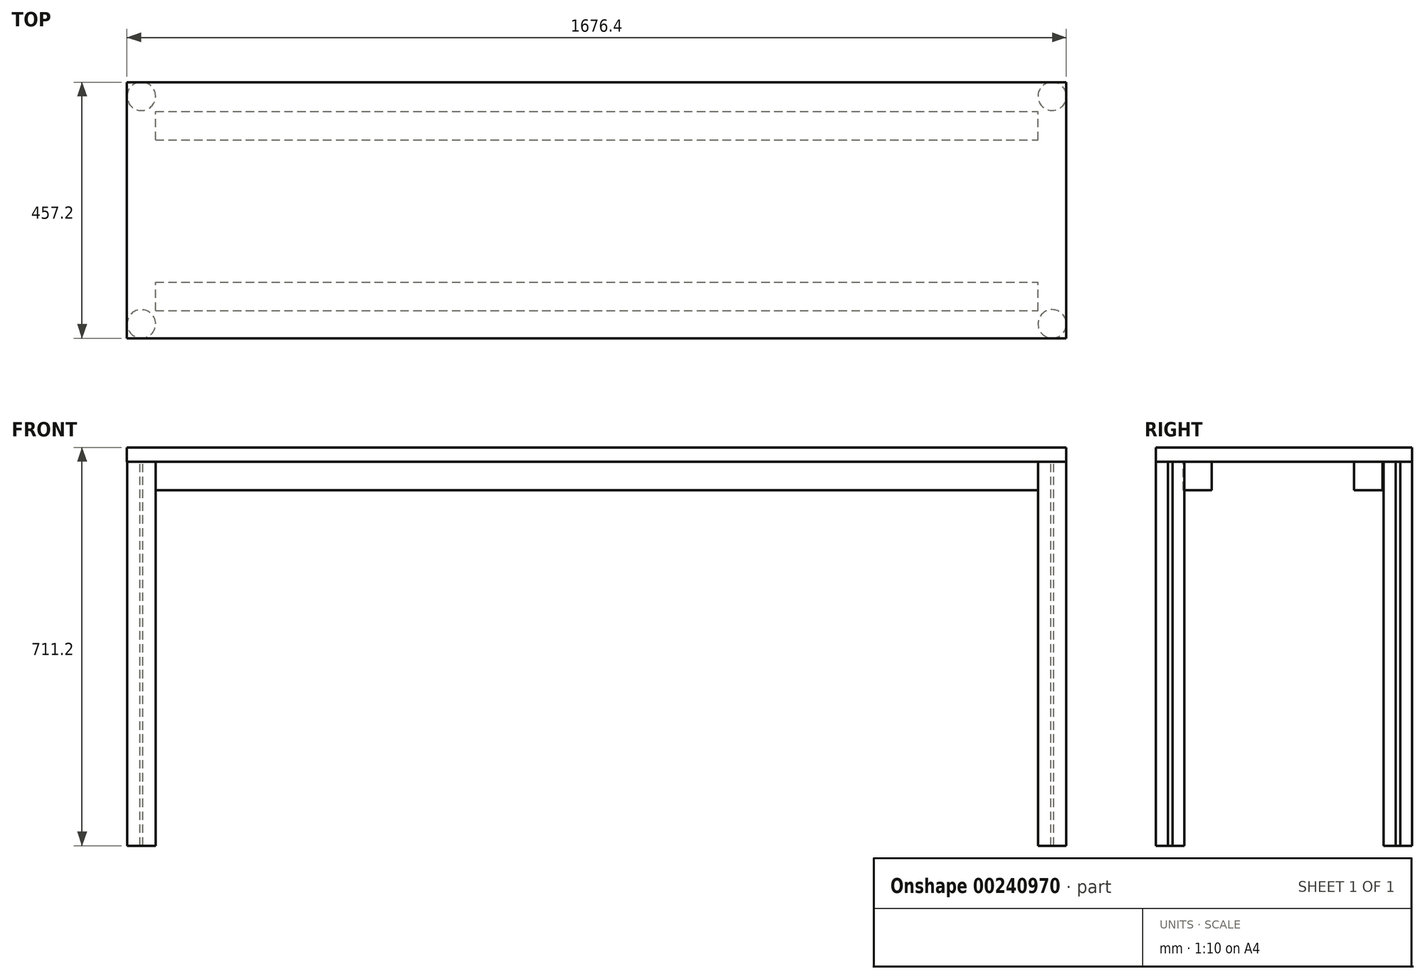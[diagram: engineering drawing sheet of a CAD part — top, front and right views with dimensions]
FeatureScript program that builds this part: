
annotation { "Feature Type Name" : "Feature", "Feature Type Description" : "" }
export const myFeature = defineFeature(function(context is Context, id is Id, definition is map)
    precondition{}
    {
        {
            var Q0;
            Q0=qCreatedBy(makeId("Top.planeOp"),FACE);
            var sketch = newSketch(context, id + "F0", { "sketchPlane" : qUnion([Q0])});
            skLineSegment(sketch, "E0.bottom", {"start": v(-1681, -104.49) * mm, "end": v(-4.6, -104.49) * mm});
            skLineSegment(sketch, "E0.top", {"start": v(-1681, -561.69) * mm, "end": v(-4.6, -561.69) * mm});
            skLineSegment(sketch, "E0.left", {"start": v(-1681, -104.49) * mm, "end": v(-1681, -561.69) * mm});
            skLineSegment(sketch, "E0.right", {"start": v(-4.6, -104.49) * mm, "end": v(-4.6, -561.69) * mm});
            skSolve(sketch);
        }
        {
            var Q0;
            Q0=makeQuery(id+"F0.imprint","IMPRINT",FACE,{"disambiguationData":[TD([[makeQuery(id+"F0.imprint","IMPRINT",EDGE,{"derivedFrom":sQuery(id+"F0.wireOp",EDGE,"E0.bottom")}),-1.0]])]});
            extrude(context, id + "F1", {"entities" : qUnion([Q0]), "depth" : 25.4 * mm});
        }
        {
            var Q0;
            Q0=makeQuery(id+"F0.imprint","IMPRINT",FACE,{"disambiguationData":[TD([[makeQuery(id+"F0.imprint","IMPRINT",EDGE,{"derivedFrom":sQuery(id+"F0.wireOp",EDGE,"E0.bottom")}),-1.0]])]});
            var sketch = newSketch(context, id + "F2", { "sketchPlane" : qUnion([Q0])});
            skCircle(sketch, "E1", {"center": v(-1655.24, -536.17) * mm, "radius": 25.4 * mm});
            skCircle(sketch, "E2.0.1.0", {"center": v(-1655.24, -129.77) * mm, "radius": 25.4 * mm});
            skCircle(sketch, "E2.1.0.0", {"center": v(-29.64, -536.17) * mm, "radius": 25.4 * mm});
            skCircle(sketch, "E2.1.1.0", {"center": v(-29.64, -129.77) * mm, "radius": 25.4 * mm});
            skLineSegment(sketch, "E2.direction1", {"start": v(-1655.24, -536.17) * mm, "end": v(-29.64, -536.17) * mm, "construction": true});
            skLineSegment(sketch, "E2.direction2", {"start": v(-1655.24, -536.17) * mm, "end": v(-1655.24, -129.77) * mm, "construction": true});
            skSolve(sketch);
        }
        {
            var Q0;
            {var subQ0=sQuery(id+"F2.wireOp",EDGE,"E2.0.1.0");var subQ1=makeQuery(id+"F0.imprint","IMPRINT",EDGE,{"derivedFrom":sQuery(id+"F0.wireOp",EDGE,"E0.bottom")});var subQ2=makeQuery(id+"F2.imprint","INTERSECT",VERTEX,{"disambiguationData":[OD(0.0)],"derivedFrom":[subQ1,subQ0]});Q0=makeQuery(id+"F2.imprint","IMPRINT",FACE,{"disambiguationData":[TD([[makeQuery(id+"F2.imprint","IMPRINT",EDGE,{"disambiguationData":[TD([[subQ2,-1.0]])],"derivedFrom":subQ0}),1.0]])]});}
            var Q1;
            Q1=makeQuery(id+"F2.imprint","IMPRINT",FACE,{"disambiguationData":[TD([[makeQuery(id+"F2.imprint","IMPRINT",EDGE,{"derivedFrom":sQuery(id+"F2.wireOp",EDGE,"E1")}),1.0]])]});
            var Q2;
            {var subQ0=sQuery(id+"F2.wireOp",EDGE,"E2.1.1.0");var subQ1=makeQuery(id+"F0.imprint","IMPRINT",EDGE,{"derivedFrom":sQuery(id+"F0.wireOp",EDGE,"E0.bottom")});var subQ2=makeQuery(id+"F2.imprint","INTERSECT",VERTEX,{"disambiguationData":[OD(0.0)],"derivedFrom":[subQ1,subQ0]});Q2=makeQuery(id+"F2.imprint","IMPRINT",FACE,{"disambiguationData":[TD([[makeQuery(id+"F2.imprint","IMPRINT",EDGE,{"disambiguationData":[TD([[subQ2,1.0]])],"derivedFrom":subQ0}),1.0]])]});}
            var Q3;
            {var subQ0=sQuery(id+"F2.wireOp",EDGE,"E2.1.0.0");var subQ1=makeQuery(id+"F0.imprint","IMPRINT",EDGE,{"derivedFrom":sQuery(id+"F0.wireOp",EDGE,"E0.right")});var subQ2=makeQuery(id+"F2.imprint","INTERSECT",VERTEX,{"disambiguationData":[OD(0.0)],"derivedFrom":[subQ1,subQ0]});Q3=makeQuery(id+"F2.imprint","IMPRINT",FACE,{"disambiguationData":[TD([[makeQuery(id+"F2.imprint","IMPRINT",EDGE,{"disambiguationData":[TD([[subQ2,1.0]])],"derivedFrom":subQ0}),1.0]])]});}
            var Q4;
            Q4=sQuery(id+"F2.wireOp",EDGE,"E1");
            var Q5;
            Q5=sQuery(id+"F2.wireOp",EDGE,"E2.0.1.0");
            var Q6;
            Q6=sQuery(id+"F2.wireOp",EDGE,"E2.1.1.0");
            var Q7;
            Q7=sQuery(id+"F2.wireOp",EDGE,"E2.1.0.0");
            extrude(context, id + "F3", {"entities" : qUnion([Q0, Q1, Q2, Q3]), "surfaceEntities" : qUnion([Q4, Q5, Q6, Q7]), "oppositeDirection" : true, "depth" : 685.8 * mm});
        }
        {
            var Q0;
            Q0=makeQuery(id+"F0.imprint","IMPRINT",FACE,{"disambiguationData":[TD([[makeQuery(id+"F0.imprint","IMPRINT",EDGE,{"derivedFrom":sQuery(id+"F0.wireOp",EDGE,"E0.bottom")}),-1.0]])]});
            var sketch = newSketch(context, id + "F4", { "sketchPlane" : qUnion([Q0])});
            skLineSegment(sketch, "E3.bottom", {"start": v(-1629.96, -512.78) * mm, "end": v(-55.16, -512.78) * mm});
            skLineSegment(sketch, "E3.top", {"start": v(-1629.96, -461.98) * mm, "end": v(-55.16, -461.98) * mm});
            skLineSegment(sketch, "E3.left", {"start": v(-1629.96, -512.78) * mm, "end": v(-1629.96, -461.98) * mm});
            skLineSegment(sketch, "E4.0.1.0", {"start": v(-1629.96, -157.18) * mm, "end": v(-55.16, -157.18) * mm});
            skLineSegment(sketch, "E4.0.1.1", {"start": v(-1629.96, -207.98) * mm, "end": v(-1629.96, -157.18) * mm});
            skLineSegment(sketch, "E4.0.1.2", {"start": v(-1629.96, -207.98) * mm, "end": v(-55.16, -207.98) * mm});
            skLineSegment(sketch, "E4.1.0.0", {"start": v(-1604.56, -461.98) * mm, "end": v(-29.76, -461.98) * mm});
            skLineSegment(sketch, "E4.1.0.2", {"start": v(-1604.56, -512.78) * mm, "end": v(-29.76, -512.78) * mm});
            skLineSegment(sketch, "E4.1.1.0", {"start": v(-1604.56, -157.18) * mm, "end": v(-29.76, -157.18) * mm});
            skLineSegment(sketch, "E4.1.1.2", {"start": v(-1604.56, -207.98) * mm, "end": v(-29.76, -207.98) * mm});
            skLineSegment(sketch, "E4.2.0.0", {"start": v(-1579.16, -461.98) * mm, "end": v(-4.36, -461.98) * mm});
            skLineSegment(sketch, "E4.2.0.2", {"start": v(-1579.16, -512.78) * mm, "end": v(-4.36, -512.78) * mm});
            skLineSegment(sketch, "E4.2.1.0", {"start": v(-1579.16, -157.18) * mm, "end": v(-4.36, -157.18) * mm});
            skLineSegment(sketch, "E4.2.1.2", {"start": v(-1579.16, -207.98) * mm, "end": v(-4.36, -207.98) * mm});
            skLineSegment(sketch, "E4.2.1.3", {"start": v(-4.36, -207.98) * mm, "end": v(-4.36, -157.18) * mm});
            skLineSegment(sketch, "E4.direction1", {"start": v(-1629.96, -461.98) * mm, "end": v(-1604.56, -461.98) * mm, "construction": true});
            skLineSegment(sketch, "E4.direction2", {"start": v(-1629.96, -461.98) * mm, "end": v(-1629.96, -157.18) * mm, "construction": true});
            skLineSegment(sketch, "E5", {"start": v(-55.16, -512.78) * mm, "end": v(-55.16, -461.98) * mm});
            skLineSegment(sketch, "E6", {"start": v(-55.16, -207.98) * mm, "end": v(-55.16, -157.18) * mm});
            skSolve(sketch);
        }
        {
            var Q0;
            Q0=makeQuery(id+"F4.imprint","IMPRINT",FACE,{"disambiguationData":[TD([[makeQuery(id+"F4.imprint","IMPRINT",EDGE,{"derivedFrom":sQuery(id+"F4.wireOp",EDGE,"E3.bottom")}),1.0]])]});
            var Q1;
            Q1=makeQuery(id+"F4.imprint","IMPRINT",FACE,{"disambiguationData":[TD([[makeQuery(id+"F4.imprint","IMPRINT",EDGE,{"derivedFrom":sQuery(id+"F4.wireOp",EDGE,"E4.0.1.0")}),-1.0]])]});
            extrude(context, id + "F5", {"entities" : qUnion([Q0, Q1]), "operationType" : NewBodyOperationType.ADD, "oppositeDirection" : true, "depth" : 50.8 * mm});
        }
    });
